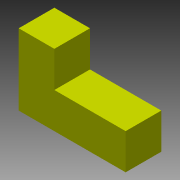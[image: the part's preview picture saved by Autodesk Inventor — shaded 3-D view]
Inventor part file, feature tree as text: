
AUTODESK INVENTOR PART (.ipt)
format: ipt  version: 2015 (Build 190159000, 159)  size: 80,384 bytes
history: native  units: in
note: dims shown in document units (in); Inventor stores cm internally (conversion verified against a paired STEP export)
features: extrude x1, sketch x1
ambient origin geometry x8: Origin, YZ Plane, XZ Plane, XY Plane, X Axis, Y Axis, Z Axis, Center Point
bodies: Solid1 (feature_tree)
feature tree (2):
  extrude  "Extrusion1"  Depth=0.75in
  sketch  "Sketch1"  dims[d0=1.5in d1=0.75in d2=0.75in d3=1.5in d4=0.75in d5=0.0in]
